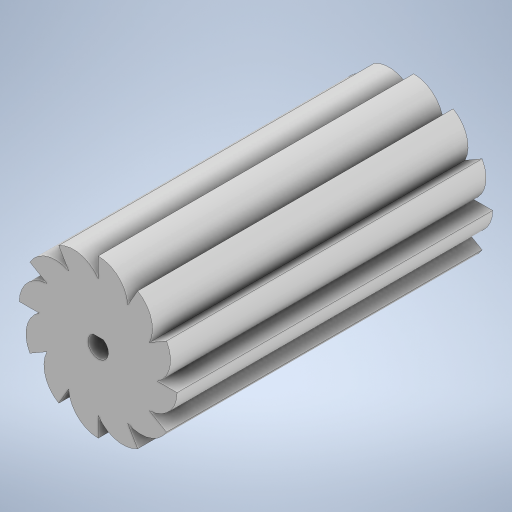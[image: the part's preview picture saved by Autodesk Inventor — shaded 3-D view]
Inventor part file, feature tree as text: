
AUTODESK INVENTOR PART (.ipt)
format: ipt  version: 2023 (Build 270158000, 158)  size: 316,416 bytes
history: native  units: in
note: dims shown in document units (in); Inventor stores cm internally (conversion verified against a paired STEP export)
features: sketch x1, extrude x1
ambient origin geometry x8: Origin, YZ Plane, XZ Plane, XY Plane, X Axis, Y Axis, Z Axis, Center Point
bodies: Solid1 (feature_tree)
feature tree (2):
  sketch  "Sketch1"  dims[d0=2.0in d1=1.5in d11=0.26in d12=4.0in d13=0.0in d17=30.0deg d18=4.7244in d20=360.0deg d27=0.13in]
  extrude  "Extrusion1"  Depth=0.13in
